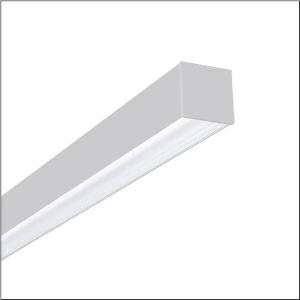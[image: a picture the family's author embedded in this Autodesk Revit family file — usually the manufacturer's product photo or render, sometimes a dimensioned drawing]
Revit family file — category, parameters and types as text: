
# Revit family: silica_r_5mx31bd2w4a_93b3
name_source: partatom
category: Lighting Fixtures
units: mm (PartAtom-declared; Revit-internal decimal feet)

## family parameters
Cut with Voids When Loaded = No
Host = Face
Light Source = No
Part Type = Normal
Room Calculation Point = No
Round Connector Dimension = Use Diameter
Shared = No

## types (1)
- --- (1 x LED, 14160 lm, 92.6 W, 4000K)
    Apparent Load = 93 VA
    CIE Flux Codes = 82 97 100 70 100
    Color Rendering = 80
    Color Temperature = 4000K
    Default Elevation = 1800 mm
    Description = Silica®, office luminaire, of aluminium, light emission: direct/indirect distribution, primary light characteristic: symmetric, installation type: suspended mounting, LED, rated luminous flux: 14.160lm, luminous efficacy: 153lm/W, light colour: 840, colour temperature: 4000K, control gear: DALI (with two DALI addresses), with terminal, 3+2-pole, max. 2.5mm², mains connection: 230V, AC, 50/60Hz, connection cable inclusive, cable length: 1,5m, rated input power: 93W, luminaire housing, of aluminium, traffic white (RAL 9016), length: 2.844mm, width: 65mm, height: 64mm, protection rating (complete): IP20, insulation class (complete): insulation class I (protective earthing), certification: CE, permissible operating ambient temperature: 0..+35°C, standard: EN 50419, packaging unit: 1 piece
    Height = 64 mm
    Lamp = 1 x LED
    Lamp Light Flux = 14160 lm
    Lamp Power = 92.6 W
    Lamp count = 1
    Length = 2845 mm
    Luminous efficacy = 153 lm/W
    Manufacturer = Siteco
    ModVariant = No
    Model = 5MX31BD2W4A
    Mounting Place = Ceiling
    Mounting Type = Pendant
    Number of Poles = 1
    OnlyDefault = Yes
    Power Factor = 1
    Product Name = Silica®
    Product group = office luminaire | ceiling pendant
    ProductGroupID = 904
    Protection Class = Protection class I
    Protection Degree = IP 20
    RLX_Detail_Level = 1
    RLX_Emergency_Light_Flux = 0 lm
    RLX_Emergency_Type = 0
    RLX_Emergency_Type_DB = No
    RlxData = <blob elided: 28933 chars, md5=f236478e>
    Socket = socket
    Standby Power = 0 W
    System Light Flux = 14160 lm
    System Power = 93 W
    Type Comments = factory setting: direct and indirect light
    Type Image = l_1003924.jpg
    URL = http://relux.com
    VarID = @adj_198505
    Voltage = 0 V
    Weight = 0.00 kg
    Width = 66 mm

## geometry (parser evidence)
native form markers: Blend x4, Sweep x13
no freeform markers — native parametric forms only
